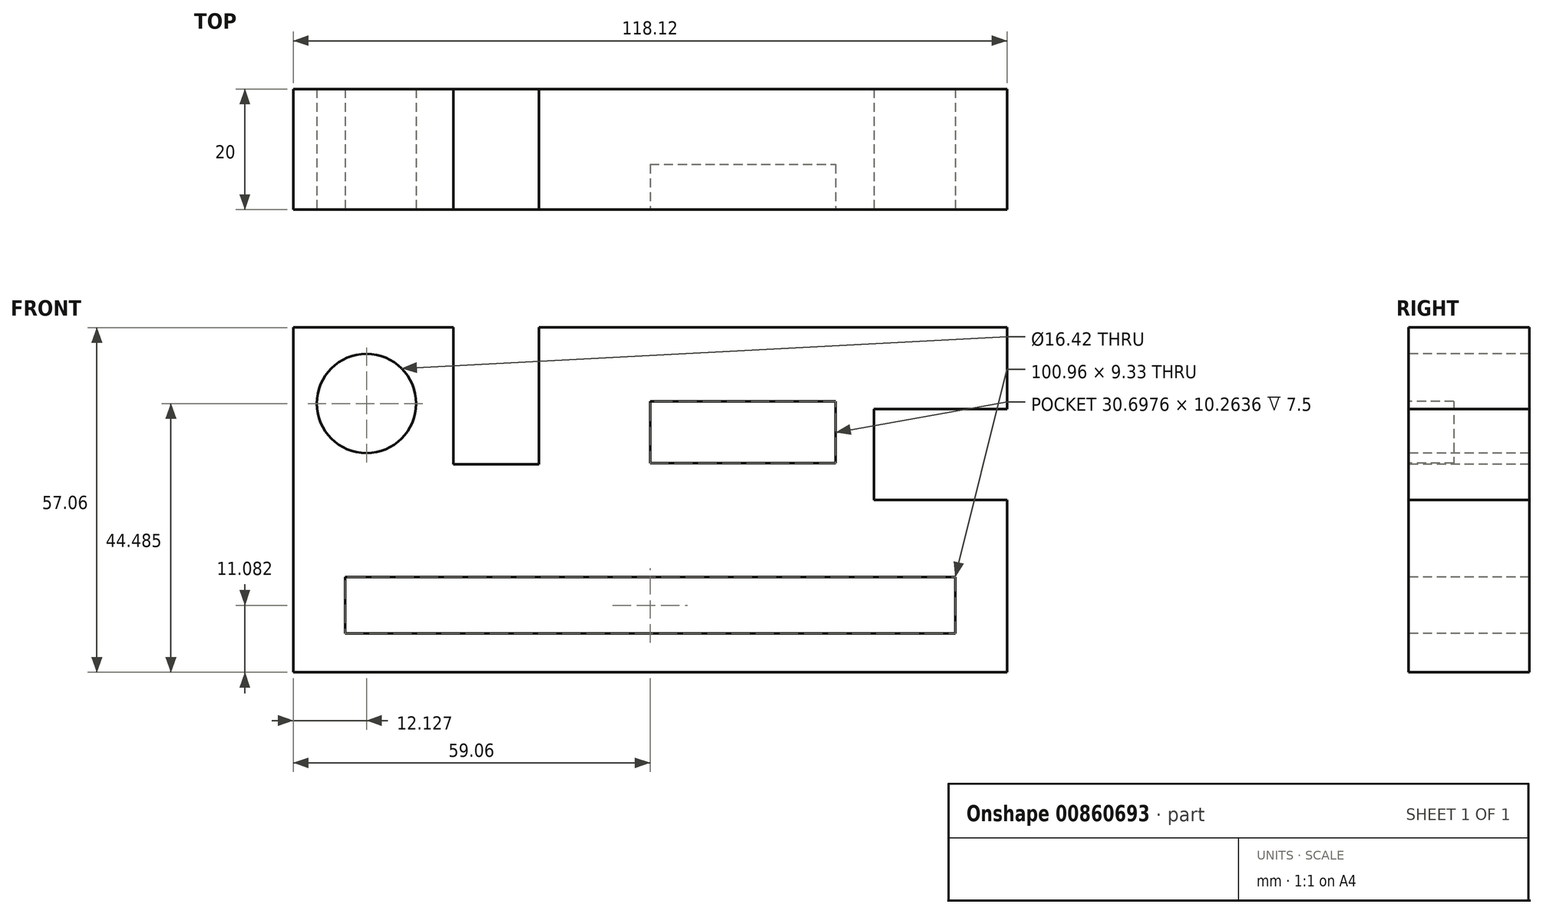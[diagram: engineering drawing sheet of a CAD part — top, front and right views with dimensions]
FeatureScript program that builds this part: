
annotation { "Feature Type Name" : "Feature", "Feature Type Description" : "" }
export const myFeature = defineFeature(function(context is Context, id is Id, definition is map)
    precondition{}
    {
        {
            var Q0;
            Q0=qCreatedBy(makeId("Front.planeOp"),FACE);
            var sketch = newSketch(context, id + "F0", { "sketchPlane" : qUnion([Q0])});
            skLineSegment(sketch, "E0.bottom", {"start": v(59.06, 28.53) * mm, "end": v(-59.06, 28.53) * mm});
            skLineSegment(sketch, "E0.top", {"start": v(59.06, -28.53) * mm, "end": v(-59.06, -28.53) * mm});
            skLineSegment(sketch, "E0.left", {"start": v(59.06, 28.53) * mm, "end": v(59.06, -28.53) * mm});
            skLineSegment(sketch, "E0.right", {"start": v(-59.06, 28.53) * mm, "end": v(-59.06, -28.53) * mm});
            skPoint(sketch, "E0.middle", {"position": v(0, 0) * mm});
            skSolve(sketch);
        }
        {
            var Q0;
            Q0=makeQuery(id+"F0.imprint","IMPRINT",FACE,{"disambiguationData":[TD([[makeQuery(id+"F0.imprint","IMPRINT",EDGE,{"derivedFrom":sQuery(id+"F0.wireOp",EDGE,"E0.bottom")}),1.0]])]});
            extrude(context, id + "F1", {"entities" : qUnion([Q0]), "depth" : 20 * mm, "offsetDistance" : 25.4 * mm});
        }
        {
            var Q0;
            Q0=makeQuery(id+"F1.opExtrude","CAP_FACE",FACE,{"disambiguationData":[OSD([sQuery(id+"F0.wireOp",EDGE,"E0.bottom"),sQuery(id+"F0.wireOp",EDGE,"E0.top"),sQuery(id+"F0.wireOp",EDGE,"E0.left"),sQuery(id+"F0.wireOp",EDGE,"E0.right")])],"isStart":false});
            var sketch = newSketch(context, id + "F2", { "sketchPlane" : qUnion([Q0])});
            skCircle(sketch, "E1", {"center": v(-46.93, 15.96) * mm, "radius": 8.21 * mm});
            skSolve(sketch);
        }
        {
            var Q0;
            Q0=makeQuery(id+"F2.imprint","IMPRINT",FACE,{"disambiguationData":[TD([[makeQuery(id+"F2.imprint","IMPRINT",EDGE,{"derivedFrom":sQuery(id+"F2.wireOp",EDGE,"E1")}),1.0]])]});
            extrude(context, id + "F3", {"entities" : qUnion([Q0]), "operationType" : NewBodyOperationType.REMOVE, "endBound" : BoundingType.THROUGH_ALL, "oppositeDirection" : true, "depth" : 25 * mm, "offsetDistance" : 25 * mm});
        }
        {
            var Q0;
            Q0=makeQuery(id+"F1.opExtrude","CAP_FACE",FACE,{"disambiguationData":[OSD([sQuery(id+"F0.wireOp",EDGE,"E0.bottom"),sQuery(id+"F0.wireOp",EDGE,"E0.top"),sQuery(id+"F0.wireOp",EDGE,"E0.left"),sQuery(id+"F0.wireOp",EDGE,"E0.right")])],"isStart":false});
            var sketch = newSketch(context, id + "F4", { "sketchPlane" : qUnion([Q0])});
            skLineSegment(sketch, "E2.bottom", {"start": v(-32.56, 28.53) * mm, "end": v(-18.38, 28.53) * mm});
            skLineSegment(sketch, "E2.top", {"start": v(-32.56, 5.88) * mm, "end": v(-18.38, 5.88) * mm});
            skLineSegment(sketch, "E2.left", {"start": v(-32.56, 28.53) * mm, "end": v(-32.56, 5.88) * mm});
            skLineSegment(sketch, "E2.right", {"start": v(-18.38, 28.53) * mm, "end": v(-18.38, 5.88) * mm});
            skSolve(sketch);
        }
        {
            var Q0;
            Q0=makeQuery(id+"F4.imprint","IMPRINT",FACE,{"disambiguationData":[TD([[makeQuery(id+"F4.imprint","IMPRINT",EDGE,{"derivedFrom":sQuery(id+"F4.wireOp",EDGE,"E2.bottom")}),1.0]])]});
            extrude(context, id + "F5", {"entities" : qUnion([Q0]), "operationType" : NewBodyOperationType.REMOVE, "endBound" : BoundingType.THROUGH_ALL, "oppositeDirection" : true, "depth" : 25 * mm, "offsetDistance" : 25 * mm});
        }
        {
            var Q0;
            Q0=makeQuery(id+"F1.opExtrude","CAP_FACE",FACE,{"disambiguationData":[OSD([sQuery(id+"F0.wireOp",EDGE,"E0.bottom"),sQuery(id+"F0.wireOp",EDGE,"E0.top"),sQuery(id+"F0.wireOp",EDGE,"E0.left"),sQuery(id+"F0.wireOp",EDGE,"E0.right")])],"isStart":false});
            var sketch = newSketch(context, id + "F6", { "sketchPlane" : qUnion([Q0])});
            skLineSegment(sketch, "E3.bottom", {"start": v(0, 16.33) * mm, "end": v(30.7, 16.33) * mm});
            skLineSegment(sketch, "E3.top", {"start": v(0, 6.06) * mm, "end": v(30.7, 6.06) * mm});
            skLineSegment(sketch, "E3.left", {"start": v(0, 16.33) * mm, "end": v(0, 6.06) * mm});
            skLineSegment(sketch, "E3.right", {"start": v(30.7, 16.33) * mm, "end": v(30.7, 6.06) * mm});
            skSolve(sketch);
        }
        {
            var Q0;
            Q0=makeQuery(id+"F6.imprint","IMPRINT",FACE,{"disambiguationData":[TD([[makeQuery(id+"F6.imprint","IMPRINT",EDGE,{"derivedFrom":sQuery(id+"F6.wireOp",EDGE,"E3.bottom")}),-1.0]])]});
            extrude(context, id + "F7", {"entities" : qUnion([Q0]), "operationType" : NewBodyOperationType.REMOVE, "oppositeDirection" : true, "depth" : 7.5 * mm, "offsetDistance" : 25 * mm});
        }
        {
            var Q0;
            Q0=makeQuery(id+"F1.opExtrude","CAP_FACE",FACE,{"disambiguationData":[OSD([sQuery(id+"F0.wireOp",EDGE,"E0.bottom"),sQuery(id+"F0.wireOp",EDGE,"E0.top"),sQuery(id+"F0.wireOp",EDGE,"E0.left"),sQuery(id+"F0.wireOp",EDGE,"E0.right")])],"isStart":false});
            var sketch = newSketch(context, id + "F8", { "sketchPlane" : qUnion([Q0])});
            skLineSegment(sketch, "E4.bottom", {"start": v(59.06, 0) * mm, "end": v(37.04, 0) * mm});
            skLineSegment(sketch, "E4.top", {"start": v(59.06, 15.02) * mm, "end": v(37.04, 15.02) * mm});
            skLineSegment(sketch, "E4.left", {"start": v(59.06, 0) * mm, "end": v(59.06, 15.02) * mm});
            skLineSegment(sketch, "E4.right", {"start": v(37.04, 0) * mm, "end": v(37.04, 15.02) * mm});
            skSolve(sketch);
        }
        {
            var Q0;
            Q0=makeQuery(id+"F8.imprint","IMPRINT",FACE,{"disambiguationData":[TD([[makeQuery(id+"F8.imprint","IMPRINT",EDGE,{"derivedFrom":sQuery(id+"F8.wireOp",EDGE,"E4.bottom")}),-1.0]])]});
            extrude(context, id + "F9", {"entities" : qUnion([Q0]), "operationType" : NewBodyOperationType.REMOVE, "endBound" : BoundingType.THROUGH_ALL, "oppositeDirection" : true, "depth" : 25 * mm, "offsetDistance" : 25 * mm});
        }
        {
            var Q0;
            Q0=makeQuery(id+"F1.opExtrude","CAP_FACE",FACE,{"disambiguationData":[OSD([sQuery(id+"F0.wireOp",EDGE,"E0.bottom"),sQuery(id+"F0.wireOp",EDGE,"E0.top"),sQuery(id+"F0.wireOp",EDGE,"E0.left"),sQuery(id+"F0.wireOp",EDGE,"E0.right")])],"isStart":false});
            var sketch = newSketch(context, id + "F10", { "sketchPlane" : qUnion([Q0])});
            skLineSegment(sketch, "E5.bottom", {"start": v(50.48, -22.11) * mm, "end": v(-50.48, -22.11) * mm});
            skLineSegment(sketch, "E5.top", {"start": v(50.48, -12.78) * mm, "end": v(-50.48, -12.78) * mm});
            skLineSegment(sketch, "E5.left", {"start": v(50.48, -22.11) * mm, "end": v(50.48, -12.78) * mm});
            skLineSegment(sketch, "E5.right", {"start": v(-50.48, -22.11) * mm, "end": v(-50.48, -12.78) * mm});
            skPoint(sketch, "E5.middle", {"position": v(0, -17.45) * mm});
            skSolve(sketch);
        }
        {
            var Q0;
            Q0=makeQuery(id+"F10.imprint","IMPRINT",FACE,{"disambiguationData":[TD([[makeQuery(id+"F10.imprint","IMPRINT",EDGE,{"derivedFrom":sQuery(id+"F10.wireOp",EDGE,"E5.bottom")}),-1.0]])]});
            extrude(context, id + "F11", {"entities" : qUnion([Q0]), "operationType" : NewBodyOperationType.REMOVE, "endBound" : BoundingType.THROUGH_ALL, "oppositeDirection" : true, "depth" : 25 * mm, "offsetDistance" : 25 * mm});
        }
    });
